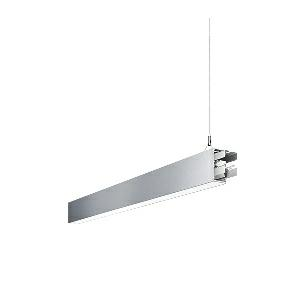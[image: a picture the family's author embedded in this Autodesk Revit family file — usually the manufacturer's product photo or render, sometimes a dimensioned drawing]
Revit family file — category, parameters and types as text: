
# Revit family: dotoo_line_-_dlp_1000_840_d_mid_00805814_c4d0
name_source: partatom
category: Lighting Fixtures
units: mm (PartAtom-declared; Revit-internal decimal feet)

## family parameters
Cut with Voids When Loaded = No
Host = Face
Light Source = No
Part Type = Normal
Room Calculation Point = No
Round Connector Dimension = Use Diameter
Shared = No

## types (1)
- DOTOO.line - DLP 1000/840/D MID (1 x LED, 1000 lm, 4000K)
    Apparent Load = 10 VA
    Approval mark = CE
    CIE Flux Codes = 67 91 98 100 100
    Color Rendering = 80-89
    Color Temperature = 4000K
    Control Gear = Electronic ballast
    Default Elevation = 1800 mm
    Description = DLP 1000/840/D|Suspended luminaire|light source: LED|connected load: 220-240 V, 50/60 Hz|Power consumption: approx. 9,5 W|standby: approx. 0,20|luminous flux: 1000 lm|luminous efficacy: 105 lm/W|light distribution: Direct|direct ratio: approx. 100 %|colour temperature: Cold white, ca. 4000 K|color rendering index (CRI): >= 80|chromaticity tolerance:  3 SDCM|System of protection: IP 40|technology: Continuously dimmable|luminaire body|material: Sectional aluminium|colour: Silver|lamp cover: Acrylic (PMMA), Clear|mains lead: 1,0 m With free stranded wires|Fastening: Steel cable 0.3 - 0.7 m|glare control: Prism aperture|luminance(L65): <= 3000 cd/m|unified glare rating(4H 8H): <=  19|special features: DALI Load 1x, TouchDIM - dimming via standard switch, Through-wired, up to 18 m on one mains connection, Flicker-free, Suitable as emergency lighting, Mechanical and electrical connection of the individual modules without tools|
    Frequency = 50 Hz
    Height = 110 mm
    Lamp = 1 x LED
    Lamp Light Flux = 1000 lm
    Lamp count = 1
    Length = 842 mm
    Luminous efficacy = 105 lm/W
    Manufacturer = Waldmann
    ModVariant = No
    Model = 00805814
    Mounting Place = Ceiling
    Mounting Type = Pendant
    Number of Poles = 1
    OnlyDefault = Yes
    Power Factor = 1
    Product Name = DOTOO.line - DLP 1000/840/D MID
    Product group = Suspended luminaire
    ProductGroupID = 9
    Protection Class = Protection class I
    Protection Degree = IP 40
    RLX_Detail_Level = 1
    RLX_Emergency_Light_Flux = 0 lm
    RLX_Emergency_Type = 0
    RLX_Emergency_Type_DB = No
    RlxData = <blob elided: 19577 chars, md5=6ef7251e>
    Socket = socket
    Standby Power = 0 W
    System Light Flux = 1000 lm
    System Power = 10 W
    Type Comments = Product without accessories
    Type Image = 113299000-00692561.jpg
    URL = http://relux.com
    VarID = ---
    Voltage = 230 V
    Voltage Range = 220-240 V
    Weight = 0.00 kg
    Width = 60 mm  [stored 0.19685 ft]

note: [stored X ft] marks values corroborated as IEEE doubles in the binary element streams (Revit-internal decimal feet)

## geometry (parser evidence)
native form markers: Blend x4, Sweep x12
no freeform markers — native parametric forms only
